# Revit family: 92002219(2023)
name_source: partatom
category: Plumbing Fixtures
units: mm (PartAtom-declared; Revit-internal decimal feet)

## family parameters
Always vertical = Yes
Cut with Voids When Loaded = No
OmniClass Number = 23.45.55.00
OmniClass Title = Sanitary Faucets, Wastes
Part Type = Normal
Room Calculation Point = No
Round Connector Dimension = Use Diameter
Shared = No
Work Plane-Based = No

## types (1)
- 92002219 Washbasin faucet, 3 V, Bluetooth
    2D/3D/BIM Files URL = http://static.hansa.com
    Advanced Features = 3S-installation system for safe and simple mounting
    Aerator = PCA® - constant flow rate regardless of pressure variations;Adjustable flow angle
    Afterflow Period = 3 s (1-20 s)
    AssetType = Fixed
    Automatic Flush Frequency = off (off/1-120 h)
    Automatic Flush Period = 30 s (1-1800 s)
    BIMObjectName = 92002219(2023)
    Backflow Prevention EN1717 = EB
    Battery = AA 1.5 V Lithium x 2
    Bluetooth = 5.x (D060576)
    BodyMaterial = Brass
    Brand = HANSA
    Catalog Drawing URL = http://static.hansa.com
    CloseOffRating = 0
    Color = Chrome
    Connection = Flexible inlet pipes
    Connection Size = G3/8
    Default Elevation = 0 mm  [stored 0 ft]
    Dimension Drawing URL = http://static.hansa.com
    DurationUnit = Year
    EAN Number = 4057304019272
    EMC Directive = 2014/53/EU , 2011/65/EU
    EN Standard = EN 15091
    ETIM Class Number = EC010340 Electronic tap
    Electrical Connection = 9 V
    Electronic Parts = ;Light indicated function(s);Low battery indicator
    FDV Document URL = http://www.hansa.com
    FaucetMainMaterial = Brass
    Features = Touchless;Battery-operated;External transformer;Bluetooth®;Lead free
    Finish = Polished
    Flow Drawing URL = http://static.hansa.com
    Flow Rate At 300kPa With Flow Controller = 0.1 L/s
    FlowCoefficient = 0
    Group = Washbasin faucet
    IfcExportAs = IfcValveType
    IfcExportType = FAUCET
    InletConnectionSize = 10 mm  [stored 0.0328084 ft]
    Installation Type = Deck mounted
    Lever Handle = Temperature control handle
    Long Marketing = Electra 92 series is giving you a whole new modern design with its rounded square body and spout. Giving you new fresh and updated design.
Design compliments the new trends of the modern bathroom with its more squared design.

Key Features
Aerator with Tilt function +/- 10° for more flexible installation
Newest Sensor technology for better detection and operation comfort
Bluetooth technology for easy adjustment to personalize settings 
Battery and power cable
    Manufacturer = HANSA
    ManufacturerName = HANSA
    ManufacturerURL = http://www.hansa.com
    Market = International;Germany;Austria;Switzerland;Belgium;Netherlands;Italy
    Material = Composite
    Max Flow Period = 2 min (1 - 1800 s)
    Max. Hot Water Supply = 70 °C
    Mechanical Parts = Mixing valve for manual temperature control;Non-return valve(s);Litter filter(s)
    Mobile Product Information URL = http://mpi.hansa.com
    Model = 92002219 Washbasin faucet, 3 V, Bluetooth
    ModelReference = 92002219
    Mounting Holes = 1 hole
    NBSDescription = Water supply fittings for wash basins and troughs
    NBSReference = 45-35-70/371
    Name = 92002219 Washbasin faucet, 3 V, Bluetooth
    Name_en = 92002219 Washbasin faucet, 3 V, Bluetooth
    Noise Class = I (ISO 3822)
    NominalDepth = 163 mm
    NominalHeight = 135 mm
    NominalWidth = 69 mm
    Operating Distance = 20-130 mm (110/130/160 mm)
    Operating Voltage = 39 V
    Product Code = 92002219
    Product Family = HANSAELECTRA
    Product Image URL = http://static.hansa.com
    Product URL = http://static.hansa.com
    Protection Class = IP 55
    Sales Package dimensions (LxWxH) = 284 x 191 x 83.5
    Shape = Sculptured
    Size = 70x165x135 mm
    Spout Projection = 117 mm
    Spout Type = Fixed spout
    Surface treatment = Chrome
    Technical DataSheet URL = http://www.hansa.com
    Temperature Adjustments = Adjustable hot water stop (included, retrofittable)
    UNSPSC Class Number = 30181700 Faucets or taps
    URL Declaration Of Performance (DOP) = http://static.hansa.com
    URL Declaration of Asbestos = http://static.hansa.com
    URL Declaration of Conformity = http://static.hansa.com
    URL Declaration of SCIP = http://static.hansa.com
    URL EU Packaging Declaration = http://static.hansa.com
    URL EcoLabel Declaration = http://static.hansa.com
    URL REACH = http://static.hansa.com
    URL UWL = http://static.hansa.com
    URL WEEE = http://static.hansa.com
    Uniclass2 = Pr_40_30_96_96
    Uniclass2015Description = Washbasin manual water supply sets
    Uniclass2015Reference = Pr_40_20_87_96
    Version = 1
    VersionDate = 01/06/2023
    Warranty Information URL = http://warranty.hansa.com
    WarrantyDescription = http://warranty.hansa.com
    WarrantyDurationUnit = Year
    Working Pressure = 100 - 1000 kPa

note: [stored X ft] marks values corroborated as IEEE doubles in the binary element streams (Revit-internal decimal feet)

## geometry (parser evidence)
native form markers: Sweep x7
no freeform markers — native parametric forms only
